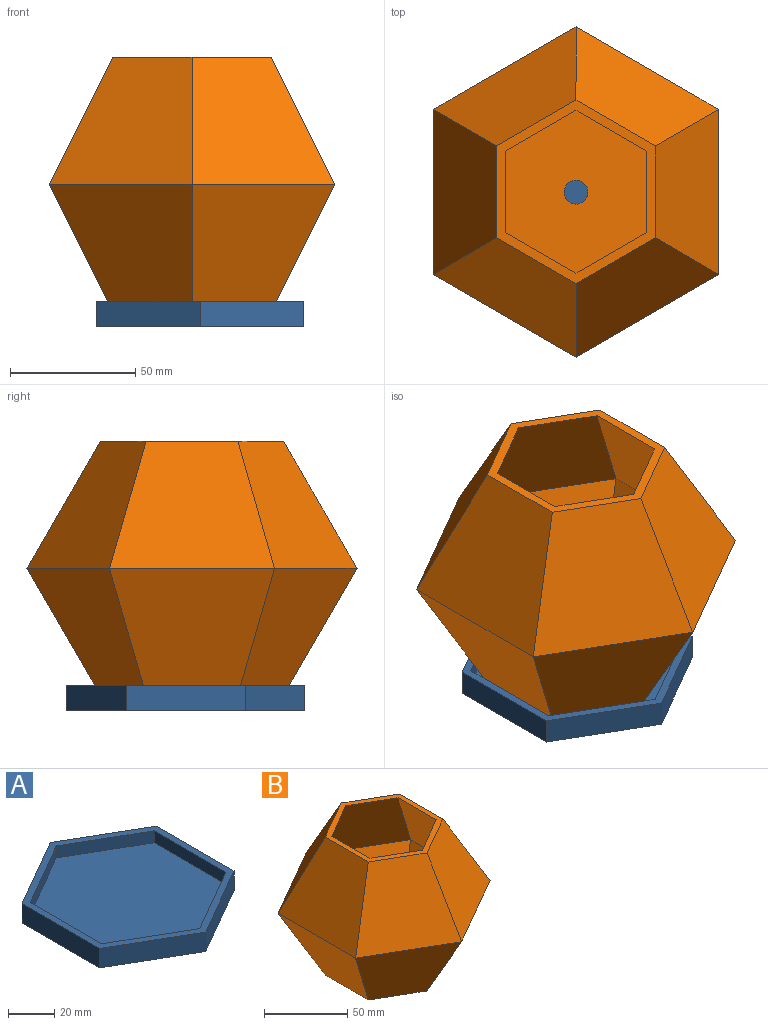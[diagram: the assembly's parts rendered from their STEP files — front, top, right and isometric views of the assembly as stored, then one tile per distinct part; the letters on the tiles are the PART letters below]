
ASSEMBLY  parts=2 mates=1
PART A: 15 faces, bbox 82.6x95.3x10.3 mm
  f0: plane 47.66x10.32mm, normal (-1,0,0), area 491.8mm2, adj f1,f5,f6,f13
  f1: plane 41.28x23.83mm, normal (-0.5,-0.87,0), area 491.8mm2, adj f0,f2,f6,f13
  f2: plane 41.28x23.83mm, normal (0.5,-0.87,0), area 491.8mm2, adj f1,f3,f6,f13
  f3: plane 47.66x10.32mm, normal (1,0,0), area 491.8mm2, adj f2,f4,f6,f13
  f4: plane 41.28x23.83mm, normal (0.5,0.87,0), area 491.8mm2, adj f3,f5,f6,f13
  f5: plane 41.28x23.83mm, normal (-0.5,0.87,0), area 491.8mm2, adj f0,f4,f6,f13
  f6: plane 95.32x82.55mm, normal (0,0,-1), area 5901.5mm2, adj f0,f1,f2,f3,f4,f5
  f7: plane 43.99x6.35mm, normal (-1,0,0), area 279.4mm2, adj f8,f12,f13,f14
  f8: plane 38.1x22mm, normal (-0.5,0.87,0), area 279.4mm2, adj f7,f9,f13,f14
  f9: plane 38.1x22mm, normal (0.5,0.87,0), area 279.4mm2, adj f8,f10,f13,f14
  f10: plane 43.99x6.35mm, normal (1,0,0), area 279.4mm2, adj f9,f11,f13,f14
  f11: plane 38.1x22mm, normal (0.5,-0.87,0), area 279.4mm2, adj f10,f12,f13,f14
  f12: plane 38.1x22mm, normal (-0.5,-0.87,0), area 279.4mm2, adj f7,f11,f13,f14
  f13: plane 95.32x82.55mm, normal (0,0,1), area 873mm2, adj f0,f1,f2,f3,f4,f5,f7,f8
  f14: plane 87.99x76.2mm, normal (0,0,1), area 5028.5mm2, adj f7,f8,f9,f10,f11,f12
PART B: 34 faces, bbox 114.3x132x101.6 mm
  f0: plane 57.15x50.73mm, normal (-0.45,-0.77,-0.45), area 2912.4mm2, adj f1,f5,f7,f28
  f1: plane 57.15x50.73mm, normal (0.45,-0.77,-0.45), area 2912.4mm2, adj f0,f2,f8,f29
  f2: plane 65.99x50.73mm, normal (0.89,0,-0.45), area 2912.4mm2, adj f1,f3,f9,f30
  f3: plane 57.15x50.73mm, normal (0.45,0.77,-0.45), area 2912.4mm2, adj f2,f4,f10,f31
  f4: plane 57.15x50.73mm, normal (-0.45,0.77,-0.45), area 2912.4mm2, adj f3,f5,f11,f32
  f5: plane 65.99x50.73mm, normal (-0.89,0,-0.45), area 2912.4mm2, adj f0,f4,f12,f27
  f6: plane 73.32x63.5mm, normal (0,0,1), area 741.5mm2, adj f7,f8,f9,f10,f11,f12,f19,f20
  f7: plane 57.15x50.8mm, normal (-0.45,-0.77,0.45), area 2915.1mm2, adj f0,f6,f8,f12
  f8: plane 57.15x50.8mm, normal (0.45,-0.77,0.45), area 2915.1mm2, adj f1,f6,f7,f9
  f9: plane 65.99x50.8mm, normal (0.89,0,0.45), area 2915.1mm2, adj f2,f6,f8,f10
  f10: plane 57.15x50.8mm, normal (0.45,0.77,0.45), area 2915.1mm2, adj f3,f6,f9,f11
  f11: plane 57.15x50.8mm, normal (-0.45,0.77,0.45), area 2915.1mm2, adj f4,f6,f10,f12
  f12: plane 65.99x50.8mm, normal (-0.89,0,0.45), area 2915.1mm2, adj f5,f6,f7,f11
  f13: plane 61.87x47.23mm, normal (0.89,0,0.45), area 2546.8mm2, adj f14,f18,f24,f26
  f14: plane 53.58x47.23mm, normal (0.45,0.77,0.45), area 2546.8mm2, adj f13,f15,f19,f26
  f15: plane 53.58x47.23mm, normal (-0.45,0.77,0.45), area 2546.8mm2, adj f14,f16,f20,f26
  f16: plane 61.87x47.23mm, normal (-0.89,0,0.45), area 2546.8mm2, adj f15,f17,f21,f26
  f17: plane 53.58x47.23mm, normal (-0.45,-0.77,0.45), area 2546.8mm2, adj f16,f18,f22,f26
  f18: plane 53.58x47.23mm, normal (0.45,-0.77,0.45), area 2546.8mm2, adj f13,f17,f23,f26
  f19: plane 53.58x50.8mm, normal (0.45,0.77,-0.45), area 2680.9mm2, adj f6,f14,f20,f24
  f20: plane 53.58x50.8mm, normal (-0.45,0.77,-0.45), area 2680.9mm2, adj f6,f15,f19,f21
  f21: plane 61.87x50.8mm, normal (-0.89,0,-0.45), area 2680.9mm2, adj f6,f16,f20,f22
  f22: plane 53.58x50.8mm, normal (-0.45,-0.77,-0.45), area 2680.9mm2, adj f6,f17,f21,f23
  f23: plane 53.58x50.8mm, normal (0.45,-0.77,-0.45), area 2680.9mm2, adj f6,f18,f22,f24
  f24: plane 61.87x50.8mm, normal (0.89,0,-0.45), area 2680.9mm2, adj f6,f13,f19,f23
  f25: cylinder r=4.76mm len=9.53mm, axis (0,0,-1), area 106.9mm2, adj f26,f33
  f26: plane 69.2x59.93mm, normal (0,0,1), area 3039mm2, adj f13,f14,f15,f16,f17,f18,f25
  f27: plane 36.7x0.07mm, normal (-1,0,0), area 2.5mm2, adj f5,f28,f32,f33
  f28: plane 31.78x18.35mm, normal (-0.5,-0.87,0), area 2.5mm2, adj f0,f27,f29,f33
  f29: plane 31.78x18.35mm, normal (0.5,-0.87,0), area 2.5mm2, adj f1,f28,f30,f33
  f30: plane 36.7x0.07mm, normal (1,0,0), area 2.5mm2, adj f2,f29,f31,f33
  f31: plane 31.78x18.35mm, normal (0.5,0.87,0), area 2.5mm2, adj f3,f30,f32,f33
  f32: plane 31.78x18.35mm, normal (-0.5,0.87,0), area 2.5mm2, adj f4,f27,f31,f33
  f33: plane 73.4x63.57mm, normal (0,0,-1), area 3428.1mm2, adj f25,f27,f28,f29,f30,f31,f32
PLACE A t=(-19.63,-18.37,-18.77)mm
PLACE B t=(-22.87,-20.92,-12.49)mm
MATE parallel B.f25 <-> A.f14  axis (0,0,-1) through (-22.87,-20.92,-12.49)mm
